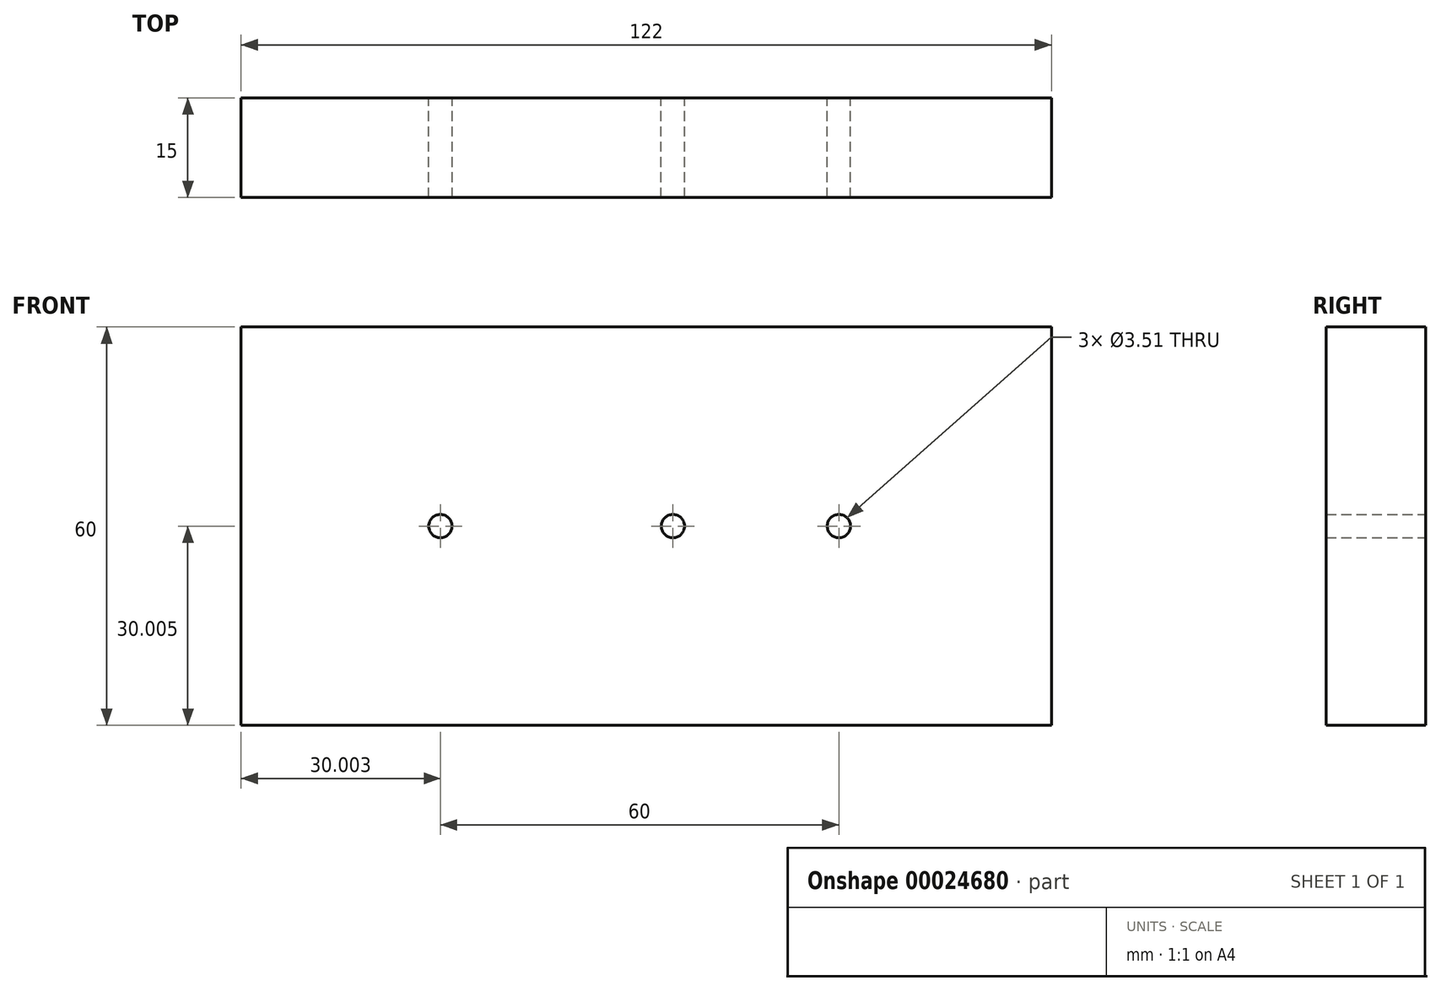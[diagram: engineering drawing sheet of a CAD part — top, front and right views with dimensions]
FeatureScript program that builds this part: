
annotation { "Feature Type Name" : "Feature", "Feature Type Description" : "" }
export const myFeature = defineFeature(function(context is Context, id is Id, definition is map)
    precondition{}
    {
        {
            var Q0;
            Q0=qCreatedBy(makeId("Front.planeOp"),FACE);
            var sketch = newSketch(context, id + "F0", { "sketchPlane" : qUnion([Q0])});
            skLineSegment(sketch, "E0.bottom", {"start": v(-115.7, 32.62) * mm, "end": v(6.3, 32.62) * mm});
            skLineSegment(sketch, "E0.top", {"start": v(-115.7, -27.38) * mm, "end": v(6.3, -27.38) * mm});
            skLineSegment(sketch, "E0.left", {"start": v(-115.7, 32.62) * mm, "end": v(-115.7, -27.38) * mm});
            skLineSegment(sketch, "E0.right", {"start": v(6.3, 32.62) * mm, "end": v(6.3, -27.38) * mm});
            skCircle(sketch, "E1", {"center": v(-85.7, 2.62) * mm, "radius": 1.75 * mm});
            skCircle(sketch, "E2", {"center": v(-50.7, 2.62) * mm, "radius": 1.75 * mm});
            skCircle(sketch, "E3", {"center": v(-25.7, 2.62) * mm, "radius": 1.75 * mm});
            skSolve(sketch);
        }
        {
            var Q0;
            Q0=makeQuery(id+"F0.imprint","IMPRINT",FACE,{"disambiguationData":[TD([[makeQuery(id+"F0.imprint","IMPRINT",EDGE,{"derivedFrom":sQuery(id+"F0.wireOp",EDGE,"E0.bottom")}),-1.0]])]});
            extrude(context, id + "F1", {"entities" : qUnion([Q0]), "depth" : 15 * mm});
        }
    });
